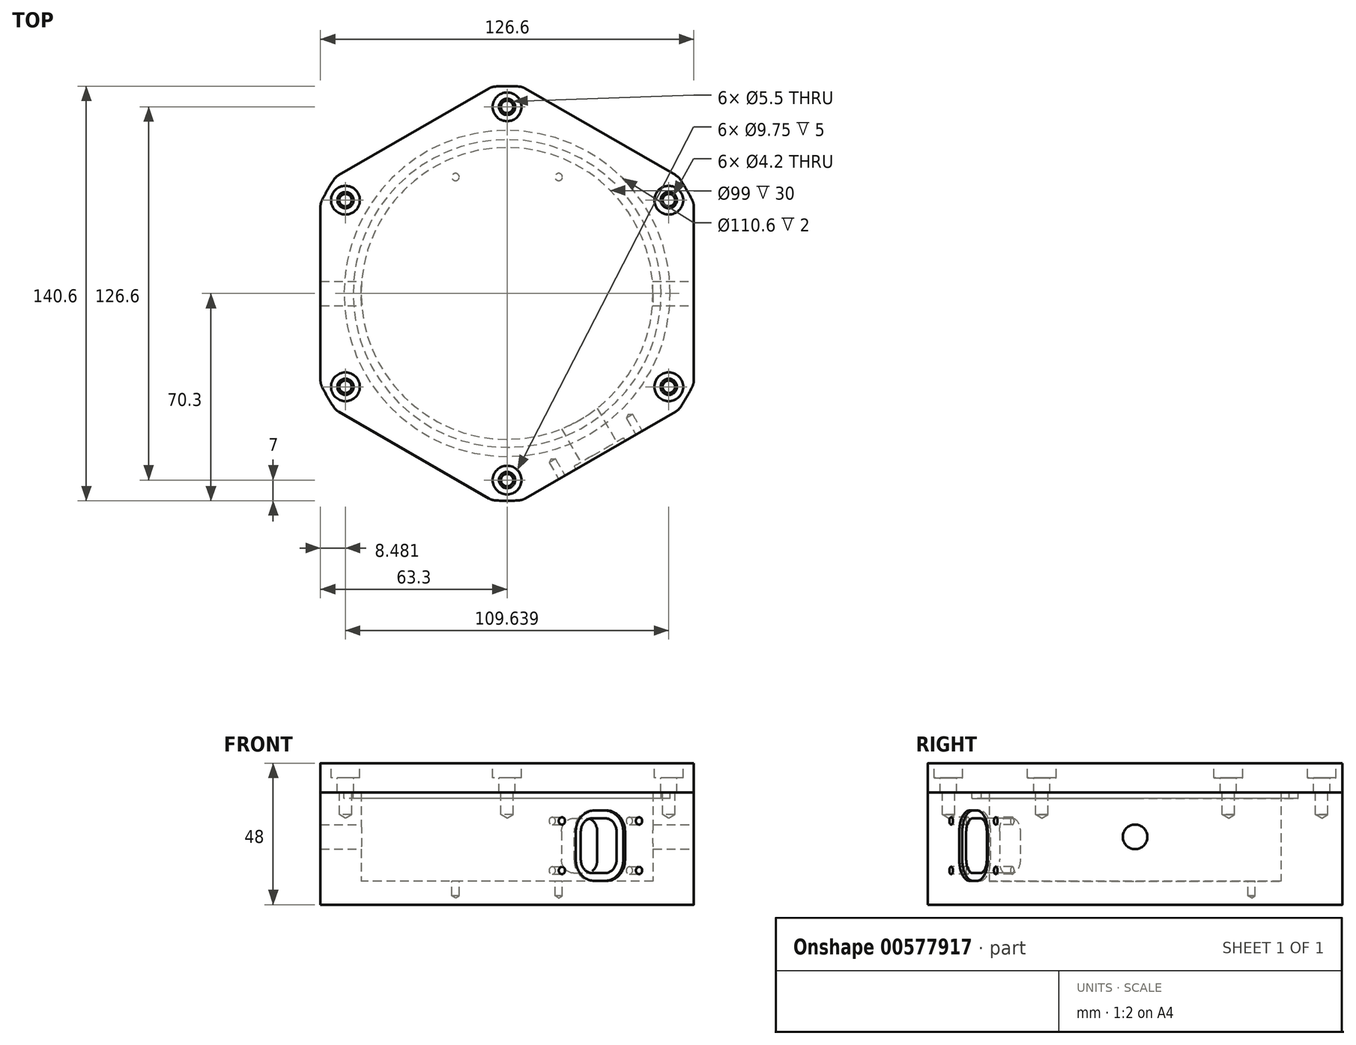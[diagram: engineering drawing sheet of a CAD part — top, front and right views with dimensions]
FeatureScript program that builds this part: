
annotation { "Feature Type Name" : "Feature", "Feature Type Description" : "" }
export const myFeature = defineFeature(function(context is Context, id is Id, definition is map)
    precondition{}
    {
        {
            var Q0;
            Q0=qCreatedBy(makeId("Top.planeOp"),FACE);
            var sketch = newSketch(context, id + "F0", { "sketchPlane" : qUnion([Q0])});
            skLineSegment(sketch, "E0.bottom", {"start": v(25, -25) * mm, "end": v(-25, -25) * mm});
            skLineSegment(sketch, "E0.top", {"start": v(25, 25) * mm, "end": v(-25, 25) * mm});
            skLineSegment(sketch, "E0.left", {"start": v(25, -25) * mm, "end": v(25, 25) * mm});
            skLineSegment(sketch, "E0.right", {"start": v(-25, -25) * mm, "end": v(-25, 25) * mm});
            skPoint(sketch, "E0.middle", {"position": v(0, 0) * mm});
            skCircle(sketch, "E1", {"center": v(0, 0) * mm, "radius": 49.5 * mm});
            skCircle(sketch, "E2", {"center": v(0, 0) * mm, "radius": 52.2 * mm});
            skCircle(sketch, "E3.0", {"center": v(0, 0) * mm, "radius": 55.3 * mm});
            skLineSegment(sketch, "E4.bottom", {"start": v(-34.5, -10) * mm, "end": v(-44.5, -10) * mm});
            skLineSegment(sketch, "E4.top", {"start": v(-34.5, 10) * mm, "end": v(-44.5, 10) * mm});
            skLineSegment(sketch, "E4.left", {"start": v(-34.5, -10) * mm, "end": v(-34.5, 10) * mm});
            skLineSegment(sketch, "E4.right", {"start": v(-44.5, -10) * mm, "end": v(-44.5, 10) * mm});
            skPoint(sketch, "E4.middle", {"position": v(-39.5, 0) * mm});
            skLineSegment(sketch, "E5", {"start": v(-70.3, 0) * mm, "end": v(70.3, 0) * mm, "construction": true});
            skLineSegment(sketch, "E6", {"start": v(0, -70.3) * mm, "end": v(0, 70.3) * mm, "construction": true});
            skCircle(sketch, "E7.0", {"center": v(0, 0) * mm, "radius": 70.3 * mm});
            skCircle(sketch, "E8.0", {"center": v(0, 0) * mm, "radius": 63.3 * mm, "construction": true});
            skLineSegment(sketch, "E9", {"start": v(0, 0) * mm, "end": v(49.7, -49.7) * mm, "construction": true});
            skPoint(sketch, "E10.orphan", {"position": v(-55.3, 0) * mm});
            skPoint(sketch, "E11.orphan", {"position": v(0, -55.3) * mm});
            skLineSegment(sketch, "E12.0", {"start": v(63.3, 36.55) * mm, "end": v(63.3, -36.55) * mm});
            skLineSegment(sketch, "E12.1", {"start": v(63.3, -36.55) * mm, "end": v(0, -73.1) * mm});
            skLineSegment(sketch, "E12.2", {"start": v(0, -73.1) * mm, "end": v(-63.3, -36.55) * mm});
            skLineSegment(sketch, "E12.3", {"start": v(-63.3, -36.55) * mm, "end": v(-63.3, 36.55) * mm});
            skLineSegment(sketch, "E12.4", {"start": v(-63.3, 36.55) * mm, "end": v(0, 73.1) * mm});
            skLineSegment(sketch, "E12.5", {"start": v(0, 73.1) * mm, "end": v(63.3, 36.55) * mm});
            skPoint(sketch, "E12.0.midPoint", {"position": v(63.3, 0) * mm});
            skLineSegment(sketch, "E13", {"start": v(0, 0) * mm, "end": v(63.3, -36.55) * mm});
            skCircle(sketch, "E14", {"center": v(54.82, -31.65) * mm, "radius": 2.58 * mm});
            skCircle(sketch, "E15.1.0", {"center": v(54.82, 31.65) * mm, "radius": 2.58 * mm});
            skCircle(sketch, "E15.2.0", {"center": v(0, 63.3) * mm, "radius": 2.58 * mm});
            skCircle(sketch, "E15.3.0", {"center": v(-54.82, 31.65) * mm, "radius": 2.58 * mm});
            skCircle(sketch, "E15.4.0", {"center": v(-54.82, -31.65) * mm, "radius": 2.58 * mm});
            skCircle(sketch, "E15.5.0", {"center": v(0, -63.3) * mm, "radius": 2.58 * mm});
            skLineSegment(sketch, "E16.bottom", {"start": v(10, 34.5) * mm, "end": v(-10, 34.5) * mm});
            skLineSegment(sketch, "E16.top", {"start": v(10, 44.5) * mm, "end": v(-10, 44.5) * mm});
            skLineSegment(sketch, "E16.left", {"start": v(10, 34.5) * mm, "end": v(10, 44.5) * mm});
            skLineSegment(sketch, "E16.right", {"start": v(-10, 34.5) * mm, "end": v(-10, 44.5) * mm});
            skPoint(sketch, "E16.middle", {"position": v(0, 39.5) * mm});
            skLineSegment(sketch, "E17", {"start": v(-17.5, 39.5) * mm, "end": v(17.5, 39.5) * mm});
            skPoint(sketch, "E17.endSnap0", {"position": v(10, 39.5) * mm});
            skCircle(sketch, "E18", {"center": v(-17.5, 39.5) * mm, "radius": 1.05 * mm});
            skCircle(sketch, "E19", {"center": v(17.5, 39.5) * mm, "radius": 1.05 * mm});
            skLineSegment(sketch, "E20.bottom", {"start": v(42.5, -15) * mm, "end": v(-42.5, -15) * mm});
            skLineSegment(sketch, "E20.top", {"start": v(42.5, 15) * mm, "end": v(-42.5, 15) * mm});
            skLineSegment(sketch, "E20.left", {"start": v(42.5, -15) * mm, "end": v(42.5, 15) * mm});
            skLineSegment(sketch, "E20.right", {"start": v(-42.5, -15) * mm, "end": v(-42.5, 15) * mm});
            skSolve(sketch);
        }
        {
            var Q0;
            Q0=sQuery(id+"F0.wireOp",EDGE,"E12.1");
            cPlane(context, id + "F1", {"entities" : qUnion([Q0]), "cplaneType" : CPlaneType.LINE_ANGLE, "offset" : 25 * mm, "angle" : 0 * degree, "width" : 150 * mm, "height" : 150 * mm});
        }
        {
            var Q0;
            Q0=qCreatedBy(id+"F1.planeOp",FACE);
            var sketch = newSketch(context, id + "F2", { "sketchPlane" : qUnion([Q0])});
            skLineSegment(sketch, "E21.bottom", {"start": v(-36.55, 30) * mm, "end": v(36.55, 30) * mm});
            skLineSegment(sketch, "E21.top", {"start": v(-36.55, 0) * mm, "end": v(36.55, 0) * mm});
            skLineSegment(sketch, "E21.left", {"start": v(-36.55, 30) * mm, "end": v(-36.55, 0) * mm});
            skLineSegment(sketch, "E21.right", {"start": v(36.55, 30) * mm, "end": v(36.55, 0) * mm});
            skLineSegment(sketch, "E22.bottom", {"start": v(15.1, 3.6) * mm, "end": v(-15.1, 3.6) * mm});
            skLineSegment(sketch, "E22.top", {"start": v(15.1, 20.4) * mm, "end": v(-15.1, 20.4) * mm});
            skLineSegment(sketch, "E22.left", {"start": v(15.1, 3.6) * mm, "end": v(15.1, 20.4) * mm});
            skLineSegment(sketch, "E22.right", {"start": v(-15.1, 3.6) * mm, "end": v(-15.1, 20.4) * mm});
            skPoint(sketch, "E22.middle", {"position": v(0, 12) * mm});
            skCircle(sketch, "E23", {"center": v(-15.1, 20.4) * mm, "radius": 1.3 * mm});
            skCircle(sketch, "E24", {"center": v(15.1, 20.4) * mm, "radius": 1.3 * mm});
            skCircle(sketch, "E25", {"center": v(-15.1, 3.6) * mm, "radius": 1.3 * mm});
            skCircle(sketch, "E26", {"center": v(15.1, 3.6) * mm, "radius": 1.3 * mm});
            skLineSegment(sketch, "E27.bottom", {"start": v(2.5, 2.7) * mm, "end": v(-2.5, 2.7) * mm});
            skLineSegment(sketch, "E27.top", {"start": v(2.5, 21.3) * mm, "end": v(-2.5, 21.3) * mm});
            skLineSegment(sketch, "E27.left", {"start": v(7, 7.2) * mm, "end": v(7, 16.8) * mm});
            skLineSegment(sketch, "E27.right", {"start": v(-7, 7.2) * mm, "end": v(-7, 16.8) * mm});
            skPoint(sketch, "E28.visualSharp", {"position": v(-7, 21.3) * mm});
            skArc(sketch, "E28.filletArc", {"start": v(-2.5, 21.3) * mm, "mid": v(-5.68, 19.98) * mm, "end": v(-7, 16.8) * mm});
            skPoint(sketch, "E29.visualSharp", {"position": v(-7, 2.7) * mm});
            skArc(sketch, "E29.filletArc", {"start": v(-7, 7.2) * mm, "mid": v(-5.68, 4.02) * mm, "end": v(-2.5, 2.7) * mm});
            skPoint(sketch, "E30.visualSharp", {"position": v(7, 2.7) * mm});
            skArc(sketch, "E30.filletArc", {"start": v(2.5, 2.7) * mm, "mid": v(5.68, 4.02) * mm, "end": v(7, 7.2) * mm});
            skPoint(sketch, "E31.visualSharp", {"position": v(7, 21.3) * mm});
            skArc(sketch, "E31.filletArc", {"start": v(7, 16.8) * mm, "mid": v(5.68, 19.98) * mm, "end": v(2.5, 21.3) * mm});
            skArc(sketch, "E32.0", {"start": v(9.62, 16.8) * mm, "mid": v(7.53, 21.83) * mm, "end": v(2.5, 23.92) * mm});
            skLineSegment(sketch, "E32.1", {"start": v(9.62, 7.2) * mm, "end": v(9.62, 16.8) * mm});
            skLineSegment(sketch, "E32.2", {"start": v(2.5, 23.92) * mm, "end": v(-2.5, 23.92) * mm});
            skArc(sketch, "E32.3", {"start": v(2.5, 0.08) * mm, "mid": v(7.53, 2.17) * mm, "end": v(9.62, 7.2) * mm});
            skArc(sketch, "E32.4", {"start": v(-2.5, 23.92) * mm, "mid": v(-7.53, 21.83) * mm, "end": v(-9.62, 16.8) * mm});
            skLineSegment(sketch, "E32.5", {"start": v(-9.62, 7.2) * mm, "end": v(-9.62, 16.8) * mm});
            skArc(sketch, "E32.6", {"start": v(-9.62, 7.2) * mm, "mid": v(-7.53, 2.17) * mm, "end": v(-2.5, 0.08) * mm});
            skLineSegment(sketch, "E32.7", {"start": v(2.5, 0.08) * mm, "end": v(-2.5, 0.08) * mm});
            skLineSegment(sketch, "E33.0", {"start": v(2.5, 22.8) * mm, "end": v(-2.5, 22.8) * mm});
            skArc(sketch, "E33.1", {"start": v(8.5, 16.8) * mm, "mid": v(6.74, 21.04) * mm, "end": v(2.5, 22.8) * mm});
            skArc(sketch, "E33.2", {"start": v(-2.5, 22.8) * mm, "mid": v(-6.74, 21.04) * mm, "end": v(-8.5, 16.8) * mm});
            skLineSegment(sketch, "E33.3", {"start": v(8.5, 7.2) * mm, "end": v(8.5, 16.8) * mm});
            skLineSegment(sketch, "E33.4", {"start": v(-8.5, 7.2) * mm, "end": v(-8.5, 16.8) * mm});
            skArc(sketch, "E33.5", {"start": v(-8.5, 7.2) * mm, "mid": v(-6.74, 2.96) * mm, "end": v(-2.5, 1.2) * mm});
            skLineSegment(sketch, "E33.6", {"start": v(2.5, 1.2) * mm, "end": v(-2.5, 1.2) * mm});
            skArc(sketch, "E33.7", {"start": v(2.5, 1.2) * mm, "mid": v(6.74, 2.96) * mm, "end": v(8.5, 7.2) * mm});
            skSolve(sketch);
        }
        {
            var Q0;
            Q0=sQuery(id+"F0.wireOp",EDGE,"E12.0");
            cPlane(context, id + "F3", {"entities" : qUnion([Q0]), "cplaneType" : CPlaneType.LINE_ANGLE, "offset" : 25 * mm, "angle" : 90 * degree, "width" : 150 * mm, "height" : 150 * mm});
        }
        {
            var Q0;
            Q0=qCreatedBy(id+"F3.planeOp",FACE);
            var sketch = newSketch(context, id + "F4", { "sketchPlane" : qUnion([Q0])});
            skLineSegment(sketch, "E34.bottom", {"start": v(-36.55, 30) * mm, "end": v(36.55, 30) * mm});
            skLineSegment(sketch, "E34.top", {"start": v(-36.55, 0) * mm, "end": v(36.55, 0) * mm});
            skLineSegment(sketch, "E34.left", {"start": v(-36.55, 30) * mm, "end": v(-36.55, 0) * mm});
            skLineSegment(sketch, "E34.right", {"start": v(36.55, 30) * mm, "end": v(36.55, 0) * mm});
            skLineSegment(sketch, "E35", {"start": v(-36.55, 15) * mm, "end": v(36.55, 15) * mm, "construction": true});
            skCircle(sketch, "E36", {"center": v(0, 15) * mm, "radius": 4.17 * mm, "construction": true});
            skSolve(sketch);
        }
        {
            var Q0;
            Q0=qCreatedBy(makeId("Top.planeOp"),FACE);
            var sketch = newSketch(context, id + "F5", { "sketchPlane" : qUnion([Q0])});
            skLineSegment(sketch, "E37.0", {"start": v(-63.3, -30.58) * mm, "end": v(-63.3, 30.58) * mm});
            skLineSegment(sketch, "E38.0", {"start": v(-58.13, 39.53) * mm, "end": v(-5.17, 70.1) * mm});
            skLineSegment(sketch, "E39.0", {"start": v(5.17, 70.1) * mm, "end": v(58.13, 39.53) * mm});
            skLineSegment(sketch, "E40.0", {"start": v(63.3, -30.58) * mm, "end": v(63.3, 30.58) * mm});
            skLineSegment(sketch, "E41.0", {"start": v(5.17, -70.1) * mm, "end": v(58.13, -39.53) * mm});
            skLineSegment(sketch, "E42.0", {"start": v(-5.17, -70.1) * mm, "end": v(-58.13, -39.53) * mm});
            skCircle(sketch, "E43.0", {"center": v(0, 0) * mm, "radius": 49.5 * mm});
            skArc(sketch, "E44.0", {"start": v(-63.3, -30.58) * mm, "mid": v(-60.88, -35.15) * mm, "end": v(-58.13, -39.53) * mm});
            skPoint(sketch, "E45.orphan", {"position": v(-63.3, 36.55) * mm});
            skArc(sketch, "E46.trimOffspring", {"start": v(-5.17, -70.1) * mm, "mid": v(0, -70.3) * mm, "end": v(5.17, -70.1) * mm});
            skArc(sketch, "E47.trimOffspring", {"start": v(58.13, -39.53) * mm, "mid": v(60.88, -35.15) * mm, "end": v(63.3, -30.58) * mm});
            skArc(sketch, "E48.trimOffspring", {"start": v(63.3, 30.58) * mm, "mid": v(60.88, 35.15) * mm, "end": v(58.13, 39.53) * mm});
            skArc(sketch, "E49.trimOffspring", {"start": v(5.17, 70.1) * mm, "mid": v(0, 70.3) * mm, "end": v(-5.17, 70.1) * mm});
            skArc(sketch, "E50.trimOffspring", {"start": v(-58.13, 39.53) * mm, "mid": v(-60.88, 35.15) * mm, "end": v(-63.3, 30.58) * mm});
            skPoint(sketch, "E51.orphan", {"position": v(0, 73.1) * mm});
            skPoint(sketch, "E52.orphan", {"position": v(63.3, 36.55) * mm});
            skPoint(sketch, "E53.orphan", {"position": v(63.3, -36.55) * mm});
            skPoint(sketch, "E54.orphan", {"position": v(0, -73.1) * mm});
            skPoint(sketch, "E55.orphan", {"position": v(-63.3, -36.55) * mm});
            skSolve(sketch);
        }
        {
            var Q0;
            Q0 = qSketchRegion(id + "F5", true);
            extrude(context, id + "F6", {"entities" : qUnion([Q0]), "depth" : 30 * mm, "offsetDistance" : 25 * mm});
        }
        {
            var Q0;
            Q0=qCreatedBy(id+"F1.planeOp",FACE);
            var sketch = newSketch(context, id + "F7", { "sketchPlane" : qUnion([Q0])});
            skArc(sketch, "E56.0", {"start": v(-2.5, 21.3) * mm, "mid": v(-5.68, 19.98) * mm, "end": v(-7, 16.8) * mm});
            skLineSegment(sketch, "E57.0", {"start": v(-7, 7.2) * mm, "end": v(-7, 16.8) * mm});
            skArc(sketch, "E58.0", {"start": v(-7, 7.2) * mm, "mid": v(-5.68, 4.02) * mm, "end": v(-2.5, 2.7) * mm});
            skLineSegment(sketch, "E59.0", {"start": v(2.5, 2.7) * mm, "end": v(-2.5, 2.7) * mm});
            skArc(sketch, "E60.0", {"start": v(2.5, 2.7) * mm, "mid": v(5.68, 4.02) * mm, "end": v(7, 7.2) * mm});
            skLineSegment(sketch, "E61.0", {"start": v(7, 7.2) * mm, "end": v(7, 16.8) * mm});
            skArc(sketch, "E62.0", {"start": v(7, 16.8) * mm, "mid": v(5.68, 19.98) * mm, "end": v(2.5, 21.3) * mm});
            skLineSegment(sketch, "E63.0", {"start": v(2.5, 21.3) * mm, "end": v(-2.5, 21.3) * mm});
            skSolve(sketch);
        }
        {
            var Q0;
            Q0 = qSketchRegion(id + "F7", true);
            extrude(context, id + "F8", {"entities" : qUnion([Q0]), "operationType" : NewBodyOperationType.REMOVE, "oppositeDirection" : true, "depth" : 25 * mm, "offsetDistance" : 25 * mm});
        }
        {
            var Q0;
            Q0=qCreatedBy(id+"F1.planeOp",FACE);
            var sketch = newSketch(context, id + "F9", { "sketchPlane" : qUnion([Q0])});
            skArc(sketch, "E64.0", {"start": v(-2.5, 23.92) * mm, "mid": v(-7.53, 21.83) * mm, "end": v(-9.62, 16.8) * mm});
            skLineSegment(sketch, "E65.0", {"start": v(-9.62, 7.2) * mm, "end": v(-9.62, 16.8) * mm});
            skArc(sketch, "E66.0", {"start": v(-9.62, 7.2) * mm, "mid": v(-7.53, 2.17) * mm, "end": v(-2.5, 0.08) * mm});
            skLineSegment(sketch, "E67.0", {"start": v(2.5, 0.08) * mm, "end": v(-2.5, 0.08) * mm});
            skArc(sketch, "E68.0", {"start": v(2.5, 0.08) * mm, "mid": v(7.53, 2.17) * mm, "end": v(9.62, 7.2) * mm});
            skLineSegment(sketch, "E69.0", {"start": v(9.62, 7.2) * mm, "end": v(9.62, 16.8) * mm});
            skArc(sketch, "E70.0", {"start": v(9.62, 16.8) * mm, "mid": v(7.53, 21.83) * mm, "end": v(2.5, 23.92) * mm});
            skLineSegment(sketch, "E71.0", {"start": v(2.5, 23.92) * mm, "end": v(-2.5, 23.92) * mm});
            skSolve(sketch);
        }
        {
            var Q0;
            Q0=qCreatedBy(makeId("Top.planeOp"),FACE);
            var sketch = newSketch(context, id + "F10", { "sketchPlane" : qUnion([Q0])});
            skLineSegment(sketch, "E72.0", {"start": v(-63.3, -30.58) * mm, "end": v(-63.3, 30.58) * mm});
            skLineSegment(sketch, "E73.0", {"start": v(-58.13, 39.53) * mm, "end": v(-5.17, 70.1) * mm});
            skLineSegment(sketch, "E74.0", {"start": v(5.17, 70.1) * mm, "end": v(58.13, 39.53) * mm});
            skLineSegment(sketch, "E75.0", {"start": v(63.3, 30.58) * mm, "end": v(63.3, -30.58) * mm});
            skLineSegment(sketch, "E76.0", {"start": v(58.13, -39.53) * mm, "end": v(5.17, -70.1) * mm});
            skArc(sketch, "E77.0", {"start": v(-5.17, -70.1) * mm, "mid": v(0, -70.3) * mm, "end": v(5.17, -70.1) * mm});
            skPoint(sketch, "E78.orphan", {"position": v(-63.3, -36.55) * mm});
            skArc(sketch, "E79.trimOffspring", {"start": v(-63.3, -30.58) * mm, "mid": v(-60.88, -35.15) * mm, "end": v(-58.13, -39.53) * mm});
            skPoint(sketch, "E80.orphan", {"position": v(-63.3, 36.55) * mm});
            skArc(sketch, "E81.trimOffspring", {"start": v(-58.13, 39.53) * mm, "mid": v(-60.88, 35.15) * mm, "end": v(-63.3, 30.58) * mm});
            skPoint(sketch, "E82.orphan", {"position": v(0, 73.1) * mm});
            skArc(sketch, "E83.trimOffspring", {"start": v(5.17, 70.1) * mm, "mid": v(0, 70.3) * mm, "end": v(-5.17, 70.1) * mm});
            skArc(sketch, "E84.trimOffspring", {"start": v(63.3, 30.58) * mm, "mid": v(60.88, 35.15) * mm, "end": v(58.13, 39.53) * mm});
            skPoint(sketch, "E85.orphan", {"position": v(63.3, 36.55) * mm});
            skPoint(sketch, "E86.orphan", {"position": v(63.3, -36.55) * mm});
            skArc(sketch, "E87.trimOffspring", {"start": v(58.13, -39.53) * mm, "mid": v(60.88, -35.15) * mm, "end": v(63.3, -30.58) * mm});
            skPoint(sketch, "E88.orphan", {"position": v(0, -73.1) * mm});
            skLineSegment(sketch, "E89.0", {"start": v(-5.17, -70.1) * mm, "end": v(-58.13, -39.53) * mm});
            skSolve(sketch);
        }
        {
            var Q0;
            Q0 = qSketchRegion(id + "F10", true);
            extrude(context, id + "F11", {"entities" : qUnion([Q0]), "operationType" : NewBodyOperationType.ADD, "oppositeDirection" : true, "depth" : 8 * mm, "offsetDistance" : 25 * mm});
        }
        {
            var Q0;
            Q0 = qSketchRegion(id + "F9", true);
            extrude(context, id + "F12", {"entities" : qUnion([Q0]), "operationType" : NewBodyOperationType.REMOVE, "oppositeDirection" : true, "depth" : 1.2 * mm, "offsetDistance" : 25 * mm});
        }
        {
            var Q0;
            Q0=sQuery(id+"F2.wireOp",VERTEX,"E22.top.end");
            var Q1;
            Q1=sQuery(id+"F2.wireOp",VERTEX,"E25.center");
            var Q2;
            Q2=sQuery(id+"F2.wireOp",VERTEX,"E26.center");
            var Q3;
            Q3=sQuery(id+"F2.wireOp",VERTEX,"E22.top.start");
            var Q4;
            Q4=makeQuery(id+"F6.opExtrude","SWEPT_BODY",BODY,{"disambiguationData":[OSD([sQuery(id+"F5.wireOp",EDGE,"E37.0"),sQuery(id+"F5.wireOp",EDGE,"E38.0"),sQuery(id+"F5.wireOp",EDGE,"E39.0"),sQuery(id+"F5.wireOp",EDGE,"E40.0"),sQuery(id+"F5.wireOp",EDGE,"E41.0"),sQuery(id+"F5.wireOp",EDGE,"E42.0"),sQuery(id+"F5.wireOp",EDGE,"E43.0"),sQuery(id+"F5.wireOp",EDGE,"E44.0"),sQuery(id+"F5.wireOp",EDGE,"E46.trimOffspring"),sQuery(id+"F5.wireOp",EDGE,"E47.trimOffspring"),sQuery(id+"F5.wireOp",EDGE,"E48.trimOffspring"),sQuery(id+"F5.wireOp",EDGE,"E49.trimOffspring"),sQuery(id+"F5.wireOp",EDGE,"E50.trimOffspring")])]});
            hole(context, id + "F13", {"style" : HoleStyle.SIMPLE, "endStyle" : HoleEndStyle.BLIND, "standardTappedOrClearance" : lookupTablePath({ "standard" : "ISO", "engagement" : "75%", "pitch" : "0.5 mm", "size" : "M3", "type" : "Tapped" }), "standardBlindInLast" : lookupTablePath({ "standard" : "ISO", "engagement" : "75%", "pitch" : "0.5 mm", "size" : "M3", "type" : "Tapped" }), "holeDiameter" : 2.5 * mm, "showTappedDepth" : true, "holeDepth" : 6.5 * mm, "isTappedThrough" : true, "tappedDepth" : 5 * mm, "tapClearance" : 3, "locations" : qUnion([Q0, Q1, Q2, Q3]), "scope" : qUnion([Q4]), "majorDiameter" : 3 * mm});
        }
        {
            var Q0;
            Q0=sQuery(id+"F4.wireOp",VERTEX,"E36.center");
            var Q1;
            Q1=makeQuery(id+"F6.opExtrude","SWEPT_BODY",BODY,{"disambiguationData":[OSD([sQuery(id+"F5.wireOp",EDGE,"E37.0"),sQuery(id+"F5.wireOp",EDGE,"E38.0"),sQuery(id+"F5.wireOp",EDGE,"E39.0"),sQuery(id+"F5.wireOp",EDGE,"E40.0"),sQuery(id+"F5.wireOp",EDGE,"E41.0"),sQuery(id+"F5.wireOp",EDGE,"E42.0"),sQuery(id+"F5.wireOp",EDGE,"E43.0"),sQuery(id+"F5.wireOp",EDGE,"E44.0"),sQuery(id+"F5.wireOp",EDGE,"E46.trimOffspring"),sQuery(id+"F5.wireOp",EDGE,"E47.trimOffspring"),sQuery(id+"F5.wireOp",EDGE,"E48.trimOffspring"),sQuery(id+"F5.wireOp",EDGE,"E49.trimOffspring"),sQuery(id+"F5.wireOp",EDGE,"E50.trimOffspring")])]});
            hole(context, id + "F14", {"style" : HoleStyle.SIMPLE, "endStyle" : HoleEndStyle.THROUGH, "holeDiameter" : 8.33 * mm, "isTappedThrough" : true, "tappedDepth" : 5 * mm, "tapClearance" : 3, "locations" : qUnion([Q0]), "scope" : qUnion([Q1])});
        }
        {
            var Q0;
            Q0=qCreatedBy(makeId("Top.planeOp"),FACE);
            cPlane(context, id + "F15", {"entities" : qUnion([Q0]), "cplaneType" : CPlaneType.OFFSET, "offset" : 30 * mm, "width" : 150 * mm, "height" : 150 * mm});
        }
        {
            var Q0;
            Q0=qCreatedBy(id+"F15.planeOp",FACE);
            var sketch = newSketch(context, id + "F16", { "sketchPlane" : qUnion([Q0])});
            skCircle(sketch, "E90.0", {"center": v(0, 0) * mm, "radius": 52.2 * mm});
            skCircle(sketch, "E91.0", {"center": v(0, 0) * mm, "radius": 55.3 * mm});
            skSolve(sketch);
        }
        {
            var Q0;
            Q0 = qSketchRegion(id + "F16", true);
            extrude(context, id + "F17", {"entities" : qUnion([Q0]), "operationType" : NewBodyOperationType.REMOVE, "oppositeDirection" : true, "depth" : 2 * mm, "offsetDistance" : 25 * mm});
        }
        {
            var Q0;
            Q0=qCreatedBy(id+"F15.planeOp",FACE);
            var sketch = newSketch(context, id + "F18", { "sketchPlane" : qUnion([Q0])});
            skPoint(sketch, "E92.0", {"position": v(-54.82, 31.65) * mm});
            skPoint(sketch, "E93.0", {"position": v(-54.82, -31.65) * mm});
            skPoint(sketch, "E94.0", {"position": v(0, -63.3) * mm});
            skPoint(sketch, "E95.0", {"position": v(54.82, -31.65) * mm});
            skPoint(sketch, "E96.0", {"position": v(54.82, 31.65) * mm});
            skPoint(sketch, "E97.0", {"position": v(0, 63.3) * mm});
            skSolve(sketch);
        }
        {
            var Q0;
            Q0=sQuery(id+"F18.wireOp",VERTEX,"E93.0");
            var Q1;
            Q1=sQuery(id+"F18.wireOp",VERTEX,"E94.0");
            var Q2;
            Q2=sQuery(id+"F18.wireOp",VERTEX,"E95.0");
            var Q3;
            Q3=sQuery(id+"F18.wireOp",VERTEX,"E97.0");
            var Q4;
            Q4=sQuery(id+"F18.wireOp",VERTEX,"E96.0");
            var Q5;
            Q5=sQuery(id+"F18.wireOp",VERTEX,"E92.0");
            var Q6;
            Q6=makeQuery(id+"F6.opExtrude","SWEPT_BODY",BODY,{"disambiguationData":[OSD([sQuery(id+"F5.wireOp",EDGE,"E37.0"),sQuery(id+"F5.wireOp",EDGE,"E38.0"),sQuery(id+"F5.wireOp",EDGE,"E39.0"),sQuery(id+"F5.wireOp",EDGE,"E40.0"),sQuery(id+"F5.wireOp",EDGE,"E41.0"),sQuery(id+"F5.wireOp",EDGE,"E42.0"),sQuery(id+"F5.wireOp",EDGE,"E43.0"),sQuery(id+"F5.wireOp",EDGE,"E44.0"),sQuery(id+"F5.wireOp",EDGE,"E46.trimOffspring"),sQuery(id+"F5.wireOp",EDGE,"E47.trimOffspring"),sQuery(id+"F5.wireOp",EDGE,"E48.trimOffspring"),sQuery(id+"F5.wireOp",EDGE,"E49.trimOffspring"),sQuery(id+"F5.wireOp",EDGE,"E50.trimOffspring")])]});
            hole(context, id + "F19", {"style" : HoleStyle.SIMPLE, "endStyle" : HoleEndStyle.BLIND, "standardTappedOrClearance" : lookupTablePath({ "standard" : "ISO", "engagement" : "75%", "pitch" : "0.8 mm", "size" : "M5", "type" : "Tapped" }), "standardBlindInLast" : lookupTablePath({ "standard" : "ISO", "engagement" : "75%", "pitch" : "0.8 mm", "size" : "M5", "type" : "Tapped" }), "holeDiameter" : 4.2 * mm, "showTappedDepth" : true, "holeDepth" : 7.4 * mm, "isTappedThrough" : true, "tappedDepth" : 5 * mm, "tapClearance" : 3, "locations" : qUnion([Q0, Q1, Q2, Q3, Q4, Q5]), "scope" : qUnion([Q6]), "majorDiameter" : 5 * mm});
        }
        {
            var Q0;
            Q0=qCreatedBy(id+"F15.planeOp",FACE);
            var sketch = newSketch(context, id + "F20", { "sketchPlane" : qUnion([Q0])});
            skArc(sketch, "E98.0", {"start": v(-58.13, 39.53) * mm, "mid": v(-60.88, 35.15) * mm, "end": v(-63.3, 30.58) * mm});
            skLineSegment(sketch, "E99.0", {"start": v(-5.17, -70.1) * mm, "end": v(-58.13, -39.53) * mm});
            skLineSegment(sketch, "E100.0", {"start": v(-63.3, -30.58) * mm, "end": v(-63.3, 30.58) * mm});
            skLineSegment(sketch, "E101.0", {"start": v(-58.13, 39.53) * mm, "end": v(-5.17, 70.1) * mm});
            skLineSegment(sketch, "E102.0", {"start": v(5.17, 70.1) * mm, "end": v(58.13, 39.53) * mm});
            skLineSegment(sketch, "E103.0", {"start": v(63.3, 30.58) * mm, "end": v(63.3, -30.58) * mm});
            skArc(sketch, "E104.trimOffspring", {"start": v(-63.3, -30.58) * mm, "mid": v(-60.88, -35.15) * mm, "end": v(-58.13, -39.53) * mm});
            skLineSegment(sketch, "E105.0", {"start": v(58.13, -39.53) * mm, "end": v(5.17, -70.1) * mm});
            skArc(sketch, "E106.trimOffspring", {"start": v(58.13, -39.53) * mm, "mid": v(60.88, -35.15) * mm, "end": v(63.3, -30.58) * mm});
            skArc(sketch, "E107.trimOffspring", {"start": v(-5.17, -70.1) * mm, "mid": v(0, -70.3) * mm, "end": v(5.17, -70.1) * mm});
            skArc(sketch, "E108.trimOffspring", {"start": v(63.3, 30.58) * mm, "mid": v(60.88, 35.15) * mm, "end": v(58.13, 39.53) * mm});
            skArc(sketch, "E109.trimOffspring", {"start": v(5.17, 70.1) * mm, "mid": v(0, 70.3) * mm, "end": v(-5.17, 70.1) * mm});
            skPoint(sketch, "E110.orphan", {"position": v(0, 73.1) * mm});
            skPoint(sketch, "E111.orphan", {"position": v(63.3, 36.55) * mm});
            skPoint(sketch, "E112.orphan", {"position": v(63.3, -36.55) * mm});
            skPoint(sketch, "E113.orphan", {"position": v(0, -73.1) * mm});
            skPoint(sketch, "E114.orphan", {"position": v(-63.3, -36.55) * mm});
            skPoint(sketch, "E115.orphan", {"position": v(-63.3, 36.55) * mm});
            skSolve(sketch);
        }
        {
            var Q0;
            Q0 = qSketchRegion(id + "F20", true);
            extrude(context, id + "F21", {"entities" : qUnion([Q0]), "depth" : 10 * mm, "offsetDistance" : 25 * mm});
        }
        {
            var Q0;
            Q0=makeQuery(id+"F21.opExtrude","CAP_FACE",FACE,{"disambiguationData":[OSD([sQuery(id+"F20.wireOp",EDGE,"E98.0"),sQuery(id+"F20.wireOp",EDGE,"E99.0"),sQuery(id+"F20.wireOp",EDGE,"E100.0"),sQuery(id+"F20.wireOp",EDGE,"E101.0"),sQuery(id+"F20.wireOp",EDGE,"E102.0"),sQuery(id+"F20.wireOp",EDGE,"E103.0"),sQuery(id+"F20.wireOp",EDGE,"E104.trimOffspring"),sQuery(id+"F20.wireOp",EDGE,"E105.0"),sQuery(id+"F20.wireOp",EDGE,"E106.trimOffspring"),sQuery(id+"F20.wireOp",EDGE,"E107.trimOffspring"),sQuery(id+"F20.wireOp",EDGE,"E108.trimOffspring"),sQuery(id+"F20.wireOp",EDGE,"E109.trimOffspring")])],"isStart":false});
            var sketch = newSketch(context, id + "F22", { "sketchPlane" : qUnion([Q0])});
            skPoint(sketch, "E116.0", {"position": v(-54.82, 31.65) * mm});
            skPoint(sketch, "E117.0", {"position": v(-54.82, -31.65) * mm});
            skPoint(sketch, "E118.0", {"position": v(0, -63.3) * mm});
            skPoint(sketch, "E119.0", {"position": v(54.82, -31.65) * mm});
            skPoint(sketch, "E120.0", {"position": v(54.82, 31.65) * mm});
            skPoint(sketch, "E121.0", {"position": v(0, 63.3) * mm});
            skSolve(sketch);
        }
        {
            var Q0;
            Q0=sQuery(id+"F22.wireOp",VERTEX,"E121.0");
            var Q1;
            Q1=sQuery(id+"F22.wireOp",VERTEX,"E116.0");
            var Q2;
            Q2=sQuery(id+"F22.wireOp",VERTEX,"E117.0");
            var Q3;
            Q3=sQuery(id+"F22.wireOp",VERTEX,"E118.0");
            var Q4;
            Q4=sQuery(id+"F22.wireOp",VERTEX,"E119.0");
            var Q5;
            Q5=sQuery(id+"F22.wireOp",VERTEX,"E120.0");
            var Q6;
            Q6=makeQuery(id+"F21.opExtrude","SWEPT_BODY",BODY,{"disambiguationData":[OSD([sQuery(id+"F20.wireOp",EDGE,"E98.0"),sQuery(id+"F20.wireOp",EDGE,"E99.0"),sQuery(id+"F20.wireOp",EDGE,"E100.0"),sQuery(id+"F20.wireOp",EDGE,"E101.0"),sQuery(id+"F20.wireOp",EDGE,"E102.0"),sQuery(id+"F20.wireOp",EDGE,"E103.0"),sQuery(id+"F20.wireOp",EDGE,"E104.trimOffspring"),sQuery(id+"F20.wireOp",EDGE,"E105.0"),sQuery(id+"F20.wireOp",EDGE,"E106.trimOffspring"),sQuery(id+"F20.wireOp",EDGE,"E107.trimOffspring"),sQuery(id+"F20.wireOp",EDGE,"E108.trimOffspring"),sQuery(id+"F20.wireOp",EDGE,"E109.trimOffspring")])]});
            hole(context, id + "F23", {"style" : HoleStyle.C_BORE, "endStyle" : HoleEndStyle.THROUGH, "standardTappedOrClearance" : lookupTablePath({ "standard" : "ISO", "fit" : "Normal", "size" : "M5", "type" : "Clearance" }), "standardBlindInLast" : lookupTablePath({ "fit" : "Standard", "standard" : "ISO", "size" : "M5", "type" : "Clearance" }), "holeDiameter" : 5.5 * mm, "cBoreDiameter" : 9.75 * mm, "cBoreDepth" : 5 * mm, "isTappedThrough" : true, "tappedDepth" : 5 * mm, "tapClearance" : 3, "locations" : qUnion([Q0, Q1, Q2, Q3, Q4, Q5]), "scope" : qUnion([Q6]), "majorDiameter" : 6 * mm});
        }
        {
            var Q0;
            Q0=makeQuery(id+"F21.opExtrude","SWEPT_EDGE",EDGE,{"disambiguationData":[OSD([sQuery(id+"F20.wireOp",EDGE,"E99.0"),sQuery(id+"F20.wireOp",EDGE,"E104.trimOffspring")])]});
            var Q1;
            Q1=makeQuery(id+"F21.opExtrude","SWEPT_EDGE",EDGE,{"disambiguationData":[OSD([sQuery(id+"F20.wireOp",EDGE,"E100.0"),sQuery(id+"F20.wireOp",EDGE,"E104.trimOffspring")])]});
            var Q2;
            Q2=makeQuery(id+"F21.opExtrude","SWEPT_EDGE",EDGE,{"disambiguationData":[OSD([sQuery(id+"F20.wireOp",EDGE,"E105.0"),sQuery(id+"F20.wireOp",EDGE,"E107.trimOffspring")])]});
            var Q3;
            Q3=makeQuery(id+"F21.opExtrude","SWEPT_EDGE",EDGE,{"disambiguationData":[OSD([sQuery(id+"F20.wireOp",EDGE,"E99.0"),sQuery(id+"F20.wireOp",EDGE,"E107.trimOffspring")])]});
            var Q4;
            Q4=makeQuery(id+"F21.opExtrude","SWEPT_EDGE",EDGE,{"disambiguationData":[OSD([sQuery(id+"F20.wireOp",EDGE,"E105.0"),sQuery(id+"F20.wireOp",EDGE,"E106.trimOffspring")])]});
            var Q5;
            Q5=makeQuery(id+"F21.opExtrude","SWEPT_EDGE",EDGE,{"disambiguationData":[OSD([sQuery(id+"F20.wireOp",EDGE,"E103.0"),sQuery(id+"F20.wireOp",EDGE,"E106.trimOffspring")])]});
            var Q6;
            Q6=makeQuery(id+"F21.opExtrude","SWEPT_EDGE",EDGE,{"disambiguationData":[OSD([sQuery(id+"F20.wireOp",EDGE,"E103.0"),sQuery(id+"F20.wireOp",EDGE,"E108.trimOffspring")])]});
            var Q7;
            Q7=makeQuery(id+"F21.opExtrude","SWEPT_EDGE",EDGE,{"disambiguationData":[OSD([sQuery(id+"F20.wireOp",EDGE,"E102.0"),sQuery(id+"F20.wireOp",EDGE,"E108.trimOffspring")])]});
            var Q8;
            Q8=makeQuery(id+"F21.opExtrude","SWEPT_EDGE",EDGE,{"disambiguationData":[OSD([sQuery(id+"F20.wireOp",EDGE,"E102.0"),sQuery(id+"F20.wireOp",EDGE,"E109.trimOffspring")])]});
            var Q9;
            Q9=makeQuery(id+"F21.opExtrude","SWEPT_EDGE",EDGE,{"disambiguationData":[OSD([sQuery(id+"F20.wireOp",EDGE,"E101.0"),sQuery(id+"F20.wireOp",EDGE,"E109.trimOffspring")])]});
            var Q10;
            Q10=makeQuery(id+"F21.opExtrude","SWEPT_EDGE",EDGE,{"disambiguationData":[OSD([sQuery(id+"F20.wireOp",EDGE,"E98.0"),sQuery(id+"F20.wireOp",EDGE,"E101.0")])]});
            var Q11;
            Q11=makeQuery(id+"F21.opExtrude","SWEPT_EDGE",EDGE,{"disambiguationData":[OSD([sQuery(id+"F20.wireOp",EDGE,"E98.0"),sQuery(id+"F20.wireOp",EDGE,"E100.0")])]});
            fillet(context, id + "F24", {"entities" : qUnion([Q0, Q1, Q2, Q3, Q4, Q5, Q6, Q7, Q8, Q9, Q10, Q11]), "radius" : 5 * mm, "tangentPropagation" : true, "allowEdgeOverflow" : false});
        }
        {
            var Q0;
            Q0=makeQuery(id+"F11.boolean.opBoolean","MERGE",EDGE,{"derivedFrom":[makeQuery(id+"F6.opExtrude","SWEPT_EDGE",EDGE,{"disambiguationData":[OSD([sQuery(id+"F5.wireOp",EDGE,"E41.0"),sQuery(id+"F5.wireOp",EDGE,"E46.trimOffspring")])]}),makeQuery(id+"F11.opExtrude","SWEPT_EDGE",EDGE,{"disambiguationData":[OSD([sQuery(id+"F10.wireOp",EDGE,"E76.0"),sQuery(id+"F10.wireOp",EDGE,"E77.0")])]})]});
            var Q1;
            Q1=makeQuery(id+"F11.boolean.opBoolean","MERGE",EDGE,{"derivedFrom":[makeQuery(id+"F6.opExtrude","SWEPT_EDGE",EDGE,{"disambiguationData":[OSD([sQuery(id+"F5.wireOp",EDGE,"E42.0"),sQuery(id+"F5.wireOp",EDGE,"E46.trimOffspring")])]}),makeQuery(id+"F11.opExtrude","SWEPT_EDGE",EDGE,{"disambiguationData":[OSD([sQuery(id+"F10.wireOp",EDGE,"E77.0"),sQuery(id+"F10.wireOp",EDGE,"E89.0")])]})]});
            var Q2;
            Q2=makeQuery(id+"F11.boolean.opBoolean","MERGE",EDGE,{"derivedFrom":[makeQuery(id+"F6.opExtrude","SWEPT_EDGE",EDGE,{"disambiguationData":[OSD([sQuery(id+"F5.wireOp",EDGE,"E41.0"),sQuery(id+"F5.wireOp",EDGE,"E47.trimOffspring")])]}),makeQuery(id+"F11.opExtrude","SWEPT_EDGE",EDGE,{"disambiguationData":[OSD([sQuery(id+"F10.wireOp",EDGE,"E76.0"),sQuery(id+"F10.wireOp",EDGE,"E87.trimOffspring")])]})]});
            var Q3;
            Q3=makeQuery(id+"F11.boolean.opBoolean","MERGE",EDGE,{"derivedFrom":[makeQuery(id+"F6.opExtrude","SWEPT_EDGE",EDGE,{"disambiguationData":[OSD([sQuery(id+"F5.wireOp",EDGE,"E40.0"),sQuery(id+"F5.wireOp",EDGE,"E47.trimOffspring")])]}),makeQuery(id+"F11.opExtrude","SWEPT_EDGE",EDGE,{"disambiguationData":[OSD([sQuery(id+"F10.wireOp",EDGE,"E75.0"),sQuery(id+"F10.wireOp",EDGE,"E87.trimOffspring")])]})]});
            var Q4;
            Q4=makeQuery(id+"F11.boolean.opBoolean","MERGE",EDGE,{"derivedFrom":[makeQuery(id+"F6.opExtrude","SWEPT_EDGE",EDGE,{"disambiguationData":[OSD([sQuery(id+"F5.wireOp",EDGE,"E40.0"),sQuery(id+"F5.wireOp",EDGE,"E48.trimOffspring")])]}),makeQuery(id+"F11.opExtrude","SWEPT_EDGE",EDGE,{"disambiguationData":[OSD([sQuery(id+"F10.wireOp",EDGE,"E75.0"),sQuery(id+"F10.wireOp",EDGE,"E84.trimOffspring")])]})]});
            var Q5;
            Q5=makeQuery(id+"F11.boolean.opBoolean","MERGE",EDGE,{"derivedFrom":[makeQuery(id+"F6.opExtrude","SWEPT_EDGE",EDGE,{"disambiguationData":[OSD([sQuery(id+"F5.wireOp",EDGE,"E39.0"),sQuery(id+"F5.wireOp",EDGE,"E48.trimOffspring")])]}),makeQuery(id+"F11.opExtrude","SWEPT_EDGE",EDGE,{"disambiguationData":[OSD([sQuery(id+"F10.wireOp",EDGE,"E74.0"),sQuery(id+"F10.wireOp",EDGE,"E84.trimOffspring")])]})]});
            var Q6;
            Q6=makeQuery(id+"F11.boolean.opBoolean","MERGE",EDGE,{"derivedFrom":[makeQuery(id+"F6.opExtrude","SWEPT_EDGE",EDGE,{"disambiguationData":[OSD([sQuery(id+"F5.wireOp",EDGE,"E39.0"),sQuery(id+"F5.wireOp",EDGE,"E49.trimOffspring")])]}),makeQuery(id+"F11.opExtrude","SWEPT_EDGE",EDGE,{"disambiguationData":[OSD([sQuery(id+"F10.wireOp",EDGE,"E74.0"),sQuery(id+"F10.wireOp",EDGE,"E83.trimOffspring")])]})]});
            var Q7;
            Q7=makeQuery(id+"F11.boolean.opBoolean","MERGE",EDGE,{"derivedFrom":[makeQuery(id+"F6.opExtrude","SWEPT_EDGE",EDGE,{"disambiguationData":[OSD([sQuery(id+"F5.wireOp",EDGE,"E38.0"),sQuery(id+"F5.wireOp",EDGE,"E49.trimOffspring")])]}),makeQuery(id+"F11.opExtrude","SWEPT_EDGE",EDGE,{"disambiguationData":[OSD([sQuery(id+"F10.wireOp",EDGE,"E73.0"),sQuery(id+"F10.wireOp",EDGE,"E83.trimOffspring")])]})]});
            var Q8;
            Q8=makeQuery(id+"F11.boolean.opBoolean","MERGE",EDGE,{"derivedFrom":[makeQuery(id+"F6.opExtrude","SWEPT_EDGE",EDGE,{"disambiguationData":[OSD([sQuery(id+"F5.wireOp",EDGE,"E38.0"),sQuery(id+"F5.wireOp",EDGE,"E50.trimOffspring")])]}),makeQuery(id+"F11.opExtrude","SWEPT_EDGE",EDGE,{"disambiguationData":[OSD([sQuery(id+"F10.wireOp",EDGE,"E73.0"),sQuery(id+"F10.wireOp",EDGE,"E81.trimOffspring")])]})]});
            var Q9;
            Q9=makeQuery(id+"F11.boolean.opBoolean","MERGE",EDGE,{"derivedFrom":[makeQuery(id+"F6.opExtrude","SWEPT_EDGE",EDGE,{"disambiguationData":[OSD([sQuery(id+"F5.wireOp",EDGE,"E37.0"),sQuery(id+"F5.wireOp",EDGE,"E50.trimOffspring")])]}),makeQuery(id+"F11.opExtrude","SWEPT_EDGE",EDGE,{"disambiguationData":[OSD([sQuery(id+"F10.wireOp",EDGE,"E72.0"),sQuery(id+"F10.wireOp",EDGE,"E81.trimOffspring")])]})]});
            var Q10;
            Q10=makeQuery(id+"F11.boolean.opBoolean","MERGE",EDGE,{"derivedFrom":[makeQuery(id+"F6.opExtrude","SWEPT_EDGE",EDGE,{"disambiguationData":[OSD([sQuery(id+"F5.wireOp",EDGE,"E37.0"),sQuery(id+"F5.wireOp",EDGE,"E44.0")])]}),makeQuery(id+"F11.opExtrude","SWEPT_EDGE",EDGE,{"disambiguationData":[OSD([sQuery(id+"F10.wireOp",EDGE,"E72.0"),sQuery(id+"F10.wireOp",EDGE,"E79.trimOffspring")])]})]});
            var Q11;
            Q11=makeQuery(id+"F11.boolean.opBoolean","MERGE",EDGE,{"derivedFrom":[makeQuery(id+"F6.opExtrude","SWEPT_EDGE",EDGE,{"disambiguationData":[OSD([sQuery(id+"F5.wireOp",EDGE,"E42.0"),sQuery(id+"F5.wireOp",EDGE,"E44.0")])]}),makeQuery(id+"F11.opExtrude","SWEPT_EDGE",EDGE,{"disambiguationData":[OSD([sQuery(id+"F10.wireOp",EDGE,"E79.trimOffspring"),sQuery(id+"F10.wireOp",EDGE,"E89.0")])]})]});
            fillet(context, id + "F25", {"entities" : qUnion([Q0, Q1, Q2, Q3, Q4, Q5, Q6, Q7, Q8, Q9, Q10, Q11]), "radius" : 5 * mm, "tangentPropagation" : true, "allowEdgeOverflow" : false});
        }
        {
            var Q0;
            Q0=sQuery(id+"F0.wireOp",VERTEX,"E17.start");
            var Q1;
            Q1=sQuery(id+"F0.wireOp",VERTEX,"E19.center");
            var Q2;
            Q2=makeQuery(id+"F6.opExtrude","SWEPT_BODY",BODY,{"disambiguationData":[OSD([sQuery(id+"F5.wireOp",EDGE,"E37.0"),sQuery(id+"F5.wireOp",EDGE,"E38.0"),sQuery(id+"F5.wireOp",EDGE,"E39.0"),sQuery(id+"F5.wireOp",EDGE,"E40.0"),sQuery(id+"F5.wireOp",EDGE,"E41.0"),sQuery(id+"F5.wireOp",EDGE,"E42.0"),sQuery(id+"F5.wireOp",EDGE,"E43.0"),sQuery(id+"F5.wireOp",EDGE,"E44.0"),sQuery(id+"F5.wireOp",EDGE,"E46.trimOffspring"),sQuery(id+"F5.wireOp",EDGE,"E47.trimOffspring"),sQuery(id+"F5.wireOp",EDGE,"E48.trimOffspring"),sQuery(id+"F5.wireOp",EDGE,"E49.trimOffspring"),sQuery(id+"F5.wireOp",EDGE,"E50.trimOffspring")])]});
            hole(context, id + "F26", {"style" : HoleStyle.SIMPLE, "endStyle" : HoleEndStyle.BLIND, "standardTappedOrClearance" : lookupTablePath({ "standard" : "ISO", "engagement" : "75%", "pitch" : "0.5 mm", "size" : "M3", "type" : "Tapped" }), "standardBlindInLast" : lookupTablePath({ "standard" : "ISO", "engagement" : "75%", "pitch" : "0.5 mm", "size" : "M3", "type" : "Tapped" }), "holeDiameter" : 2.5 * mm, "majorDiameter" : 3 * mm, "showTappedDepth" : true, "holeDepth" : 5 * mm, "isTappedThrough" : true, "tappedDepth" : 3.5 * mm, "tapClearance" : 3, "locations" : qUnion([Q0, Q1]), "scope" : qUnion([Q2])});
        }
    });
